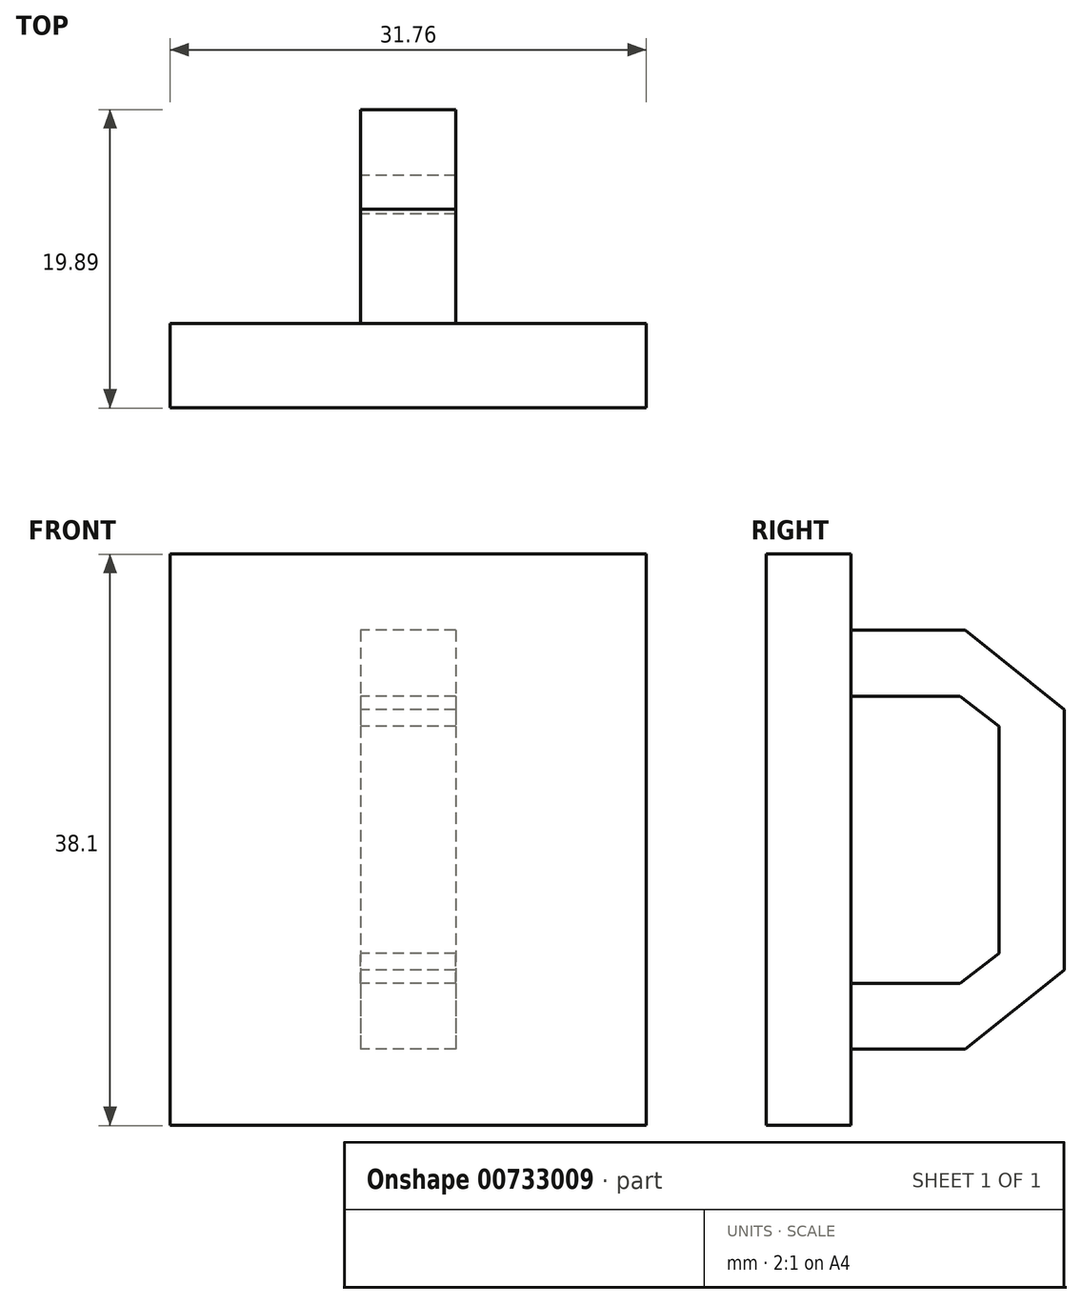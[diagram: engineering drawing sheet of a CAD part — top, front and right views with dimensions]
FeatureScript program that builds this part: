
annotation { "Feature Type Name" : "Feature", "Feature Type Description" : "" }
export const myFeature = defineFeature(function(context is Context, id is Id, definition is map)
    precondition{}
    {
        {
            var Q0;
            Q0=qCreatedBy(makeId("Right.planeOp"),FACE);
            var sketch = newSketch(context, id + "F0", { "sketchPlane" : qUnion([Q0])});
            skLineSegment(sketch, "E0", {"start": v(-23.59, 52.8) * mm, "end": v(-23.59, 14.7) * mm});
            skLineSegment(sketch, "E1", {"start": v(-23.59, 52.8) * mm, "end": v(-17.94, 52.8) * mm});
            skLineSegment(sketch, "E2", {"start": v(-17.94, 52.8) * mm, "end": v(-17.94, 14.7) * mm});
            skLineSegment(sketch, "E3", {"start": v(-17.94, 14.7) * mm, "end": v(-23.59, 14.7) * mm});
            skLineSegment(sketch, "E4", {"start": v(-17.94, 47.71) * mm, "end": v(-10.32, 47.71) * mm});
            skLineSegment(sketch, "E5", {"start": v(-17.94, 19.77) * mm, "end": v(-10.32, 19.77) * mm});
            skLineSegment(sketch, "E6", {"start": v(-10.32, 47.71) * mm, "end": v(-3.7, 42.44) * mm});
            skLineSegment(sketch, "E7", {"start": v(-3.7, 25.05) * mm, "end": v(-10.32, 19.77) * mm});
            skLineSegment(sketch, "E8", {"start": v(-3.7, 42.44) * mm, "end": v(-3.7, 25.05) * mm});
            skLineSegment(sketch, "E9", {"start": v(-17.94, 43.32) * mm, "end": v(-10.67, 43.32) * mm});
            skLineSegment(sketch, "E10", {"start": v(-10.67, 43.32) * mm, "end": v(-8.06, 41.31) * mm});
            skLineSegment(sketch, "E11", {"start": v(-17.94, 24.17) * mm, "end": v(-10.67, 24.17) * mm});
            skLineSegment(sketch, "E12", {"start": v(-10.67, 24.17) * mm, "end": v(-8.06, 26.18) * mm});
            skLineSegment(sketch, "E13", {"start": v(-8.06, 41.31) * mm, "end": v(-8.06, 26.18) * mm});
            skSolve(sketch);
        }
        {
            var Q0;
            Q0=makeQuery(id+"F0.imprint","IMPRINT",FACE,{"disambiguationData":[TD([[makeQuery(id+"F0.imprint","IMPRINT",EDGE,{"derivedFrom":sQuery(id+"F0.wireOp",EDGE,"E0")}),1.0]])]});
            extrude(context, id + "F1", {"entities" : qUnion([Q0]), "endBound" : BoundingType.SYMMETRIC, "depth" : 31.75 * mm, "offsetDistance" : 25.4 * mm});
        }
        {
            var Q0;
            {var subQ2=sQuery(id+"F0.wireOp",EDGE,"E4");Q0=makeQuery(id+"F0.imprint","IMPRINT",FACE,{"disambiguationData":[TD([[makeQuery(id+"F0.imprint","IMPRINT",EDGE,{"derivedFrom":subQ2}),-1.0]])]});}
            extrude(context, id + "F2", {"entities" : qUnion([Q0]), "operationType" : NewBodyOperationType.ADD, "endBound" : BoundingType.SYMMETRIC, "depth" : 6.35 * mm, "offsetDistance" : 25.4 * mm});
        }
    });
